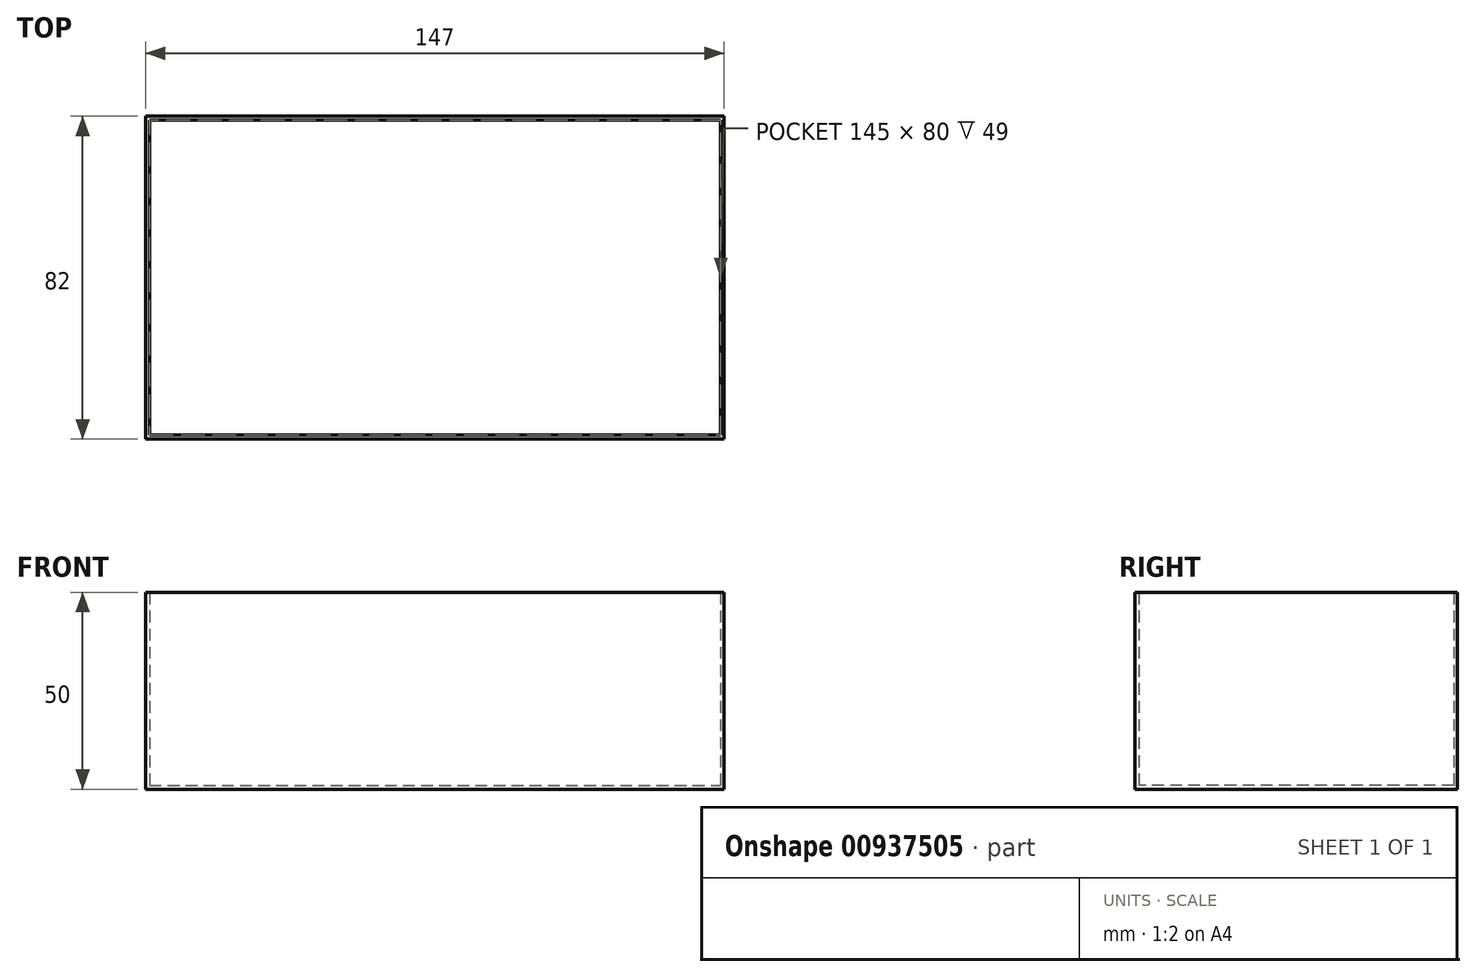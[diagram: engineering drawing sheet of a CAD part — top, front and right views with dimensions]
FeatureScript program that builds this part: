
annotation { "Feature Type Name" : "Feature", "Feature Type Description" : "" }
export const myFeature = defineFeature(function(context is Context, id is Id, definition is map)
    precondition{}
    {
        {
            var Q0;
            Q0=qCreatedBy(makeId("Top.planeOp"),FACE);
            var sketch = newSketch(context, id + "F0", { "sketchPlane" : qUnion([Q0])});
            skLineSegment(sketch, "E0.bottom", {"start": v(-168.8, -5.55) * mm, "end": v(-21.8, -5.55) * mm});
            skLineSegment(sketch, "E0.top", {"start": v(-168.8, -87.55) * mm, "end": v(-21.8, -87.55) * mm});
            skLineSegment(sketch, "E0.left", {"start": v(-168.8, -5.55) * mm, "end": v(-168.8, -87.55) * mm});
            skLineSegment(sketch, "E0.right", {"start": v(-21.8, -5.55) * mm, "end": v(-21.8, -87.55) * mm});
            skSolve(sketch);
        }
        {
            var Q0;
            Q0 = qSketchRegion(id + "F0", true);
            extrude(context, id + "F1", {"entities" : qUnion([Q0]), "depth" : 50 * mm, "offsetDistance" : 25 * mm});
        }
        {
            var Q0;
            Q0=makeQuery(id+"F1.opExtrude","CAP_FACE",FACE,{"disambiguationData":[OSD([sQuery(id+"F0.wireOp",EDGE,"E0.bottom"),sQuery(id+"F0.wireOp",EDGE,"E0.top"),sQuery(id+"F0.wireOp",EDGE,"E0.left"),sQuery(id+"F0.wireOp",EDGE,"E0.right")])],"isStart":false});
            shell(context, id + "F2", {"entities" : qUnion([Q0]), "thickness" : 1 * mm});
        }
        {
            var Q0;
            Q0=makeQuery(id+"F1.opExtrude","SWEPT_BODY",BODY,{"disambiguationData":[OSD([sQuery(id+"F0.wireOp",EDGE,"E0.bottom"),sQuery(id+"F0.wireOp",EDGE,"E0.top"),sQuery(id+"F0.wireOp",EDGE,"E0.left"),sQuery(id+"F0.wireOp",EDGE,"E0.right")])]});
            transform(context, id + "F3", {"entities" : qUnion([Q0]), "transformType" : TransformType.TRANSLATION_3D, "dx" : 38.9 * mm, "dy" : 0 * mm, "dz" : 0 * mm, "makeCopy" : false});
        }
    });
